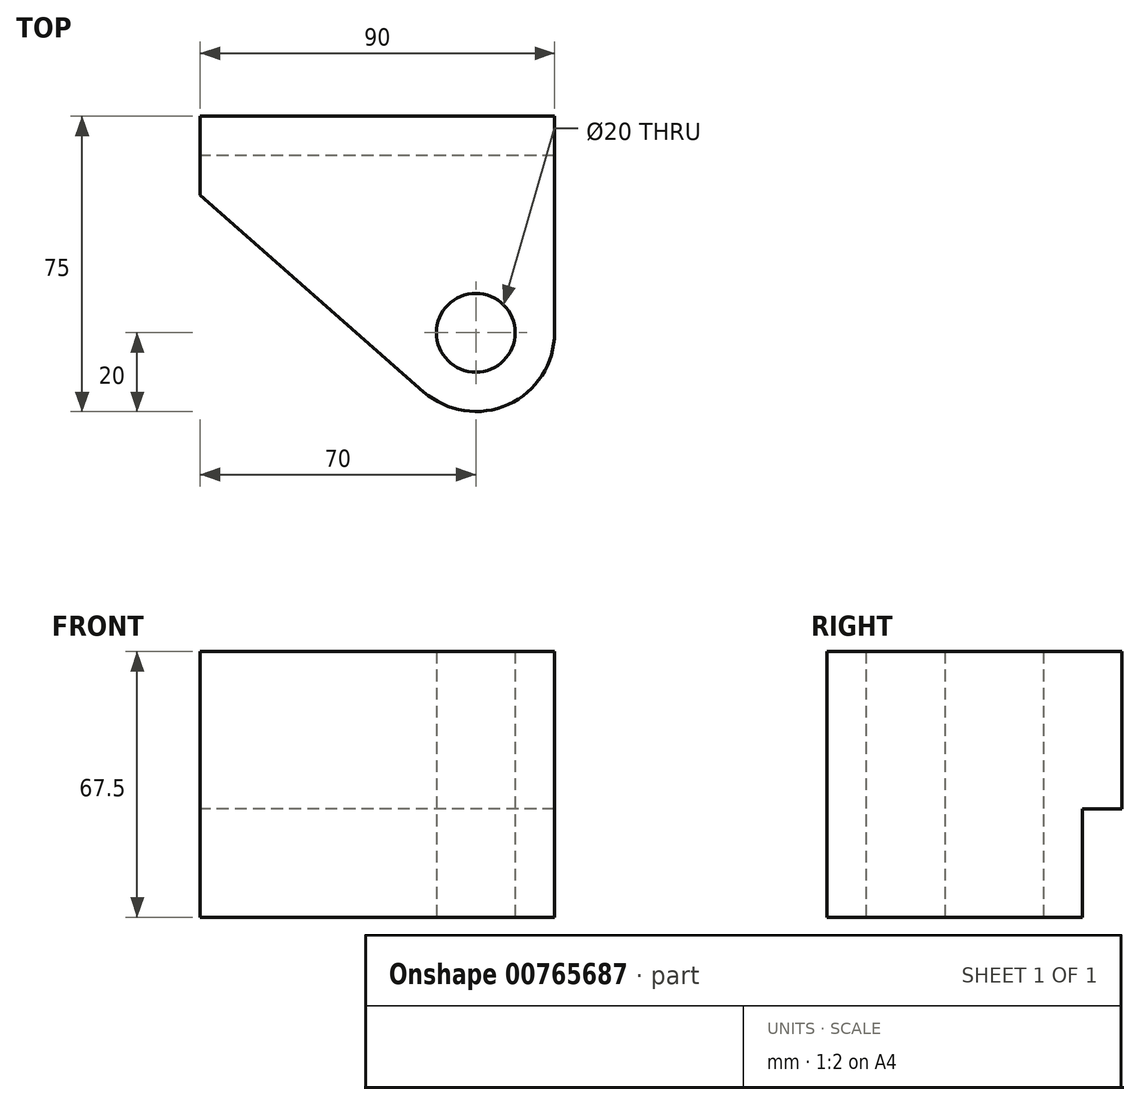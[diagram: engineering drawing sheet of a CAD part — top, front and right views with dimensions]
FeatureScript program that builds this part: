
annotation { "Feature Type Name" : "Feature", "Feature Type Description" : "" }
export const myFeature = defineFeature(function(context is Context, id is Id, definition is map)
    precondition{}
    {
        {
            var Q0;
            Q0=qCreatedBy(makeId("Top.planeOp"),FACE);
            var sketch = newSketch(context, id + "F0", { "sketchPlane" : qUnion([Q0])});
            skLineSegment(sketch, "E0.top", {"start": v(45, 37.5) * mm, "end": v(-45, 37.5) * mm});
            skLineSegment(sketch, "E0.left", {"start": v(45, -17.5) * mm, "end": v(45, 37.5) * mm});
            skPoint(sketch, "E0.middle", {"position": v(0, 0) * mm});
            skLineSegment(sketch, "E1", {"start": v(-45, 27.5) * mm, "end": v(45, 27.5) * mm});
            skLineSegment(sketch, "E2", {"start": v(-45, 17.5) * mm, "end": v(45, 17.5) * mm});
            skCircle(sketch, "E3", {"center": v(25, -17.5) * mm, "radius": 20 * mm});
            skPoint(sketch, "E4.orphan", {"position": v(45, -37.5) * mm});
            skLineSegment(sketch, "E5", {"start": v(5, 17.5) * mm, "end": v(5, -17.5) * mm});
            skLineSegment(sketch, "E6", {"start": v(-45, 17.5) * mm, "end": v(11.78, -32.5) * mm});
            skLineSegment(sketch, "E7", {"start": v(-45, 37.5) * mm, "end": v(-45, 17.5) * mm});
            skLineSegment(sketch, "E8", {"start": v(-8, 27.5) * mm, "end": v(-8, 17.5) * mm});
            skLineSegment(sketch, "E9", {"start": v(-2, 27.5) * mm, "end": v(-2, 17.5) * mm});
            skCircle(sketch, "E10", {"center": v(25, -17.5) * mm, "radius": 10 * mm});
            skSolve(sketch);
        }
        {
            var Q0;
            {var subQ5=sQuery(id+"F0.wireOp",EDGE,"E0.top");Q0=makeQuery(id+"F0.imprint","IMPRINT",FACE,{"disambiguationData":[TD([[makeQuery(id+"F0.imprint","IMPRINT",EDGE,{"derivedFrom":subQ5}),1.0]])]});}
            var Q1;
            {var subQ3=sQuery(id+"F0.wireOp",EDGE,"E8");Q1=makeQuery(id+"F0.imprint","IMPRINT",FACE,{"disambiguationData":[TD([[makeQuery(id+"F0.imprint","IMPRINT",EDGE,{"derivedFrom":subQ3}),-1.0]])]});}
            var Q2;
            {var subQ0=sQuery(id+"F0.wireOp",EDGE,"E8");Q2=makeQuery(id+"F0.imprint","IMPRINT",FACE,{"disambiguationData":[TD([[makeQuery(id+"F0.imprint","IMPRINT",EDGE,{"derivedFrom":subQ0}),1.0]])]});}
            var Q3;
            {var subQ4=sQuery(id+"F0.wireOp",EDGE,"E9");Q3=makeQuery(id+"F0.imprint","IMPRINT",FACE,{"disambiguationData":[TD([[makeQuery(id+"F0.imprint","IMPRINT",EDGE,{"derivedFrom":subQ4}),1.0]])]});}
            var Q4;
            {var subQ5=sQuery(id+"F0.wireOp",EDGE,"E5");Q4=makeQuery(id+"F0.imprint","IMPRINT",FACE,{"disambiguationData":[TD([[makeQuery(id+"F0.imprint","IMPRINT",EDGE,{"derivedFrom":subQ5}),1.0]])]});}
            var Q5;
            {var subQ0=sQuery(id+"F0.wireOp",EDGE,"E5");Q5=makeQuery(id+"F0.imprint","IMPRINT",FACE,{"disambiguationData":[TD([[makeQuery(id+"F0.imprint","IMPRINT",EDGE,{"derivedFrom":subQ0}),-1.0]])]});}
            var Q6;
            Q6=makeQuery(id+"F0.imprint","IMPRINT",FACE,{"disambiguationData":[TD([[makeQuery(id+"F0.imprint","IMPRINT",EDGE,{"derivedFrom":sQuery(id+"F0.wireOp",EDGE,"E10")}),-1.0]])]});
            extrude(context, id + "F1", {"entities" : qUnion([Q0, Q1, Q2, Q3, Q4, Q5, Q6]), "depth" : 135 / 2 * mm, "offsetDistance" : 25 * mm});
        }
        {
            var Q0;
            Q0=makeQuery(id+"F1.opExtrude","SWEPT_FACE",FACE,{"disambiguationData":[OSD([sQuery(id+"F0.wireOp",EDGE,"E7")])]});
            var sketch = newSketch(context, id + "F2", { "sketchPlane" : qUnion([Q0])});
            skLineSegment(sketch, "E11.bottom", {"start": v(-27.5, 0) * mm, "end": v(-37.5, 0) * mm});
            skLineSegment(sketch, "E11.top", {"start": v(-27.5, 27.5) * mm, "end": v(-37.5, 27.5) * mm});
            skLineSegment(sketch, "E11.left", {"start": v(-37.5, 0) * mm, "end": v(-37.5, 27.5) * mm});
            skLineSegment(sketch, "E11.right", {"start": v(-27.5, 0) * mm, "end": v(-27.5, 27.5) * mm});
            skSolve(sketch);
        }
        {
            var Q0;
            Q0=makeQuery(id+"F2.imprint","IMPRINT",FACE,{"disambiguationData":[TD([[makeQuery(id+"F2.imprint","IMPRINT",EDGE,{"derivedFrom":sQuery(id+"F2.wireOp",EDGE,"E11.bottom")}),1.0]])]});
            extrude(context, id + "F3", {"entities" : qUnion([Q0]), "operationType" : NewBodyOperationType.REMOVE, "oppositeDirection" : true, "depth" : 250 * mm, "offsetDistance" : 25 * mm});
        }
    });
